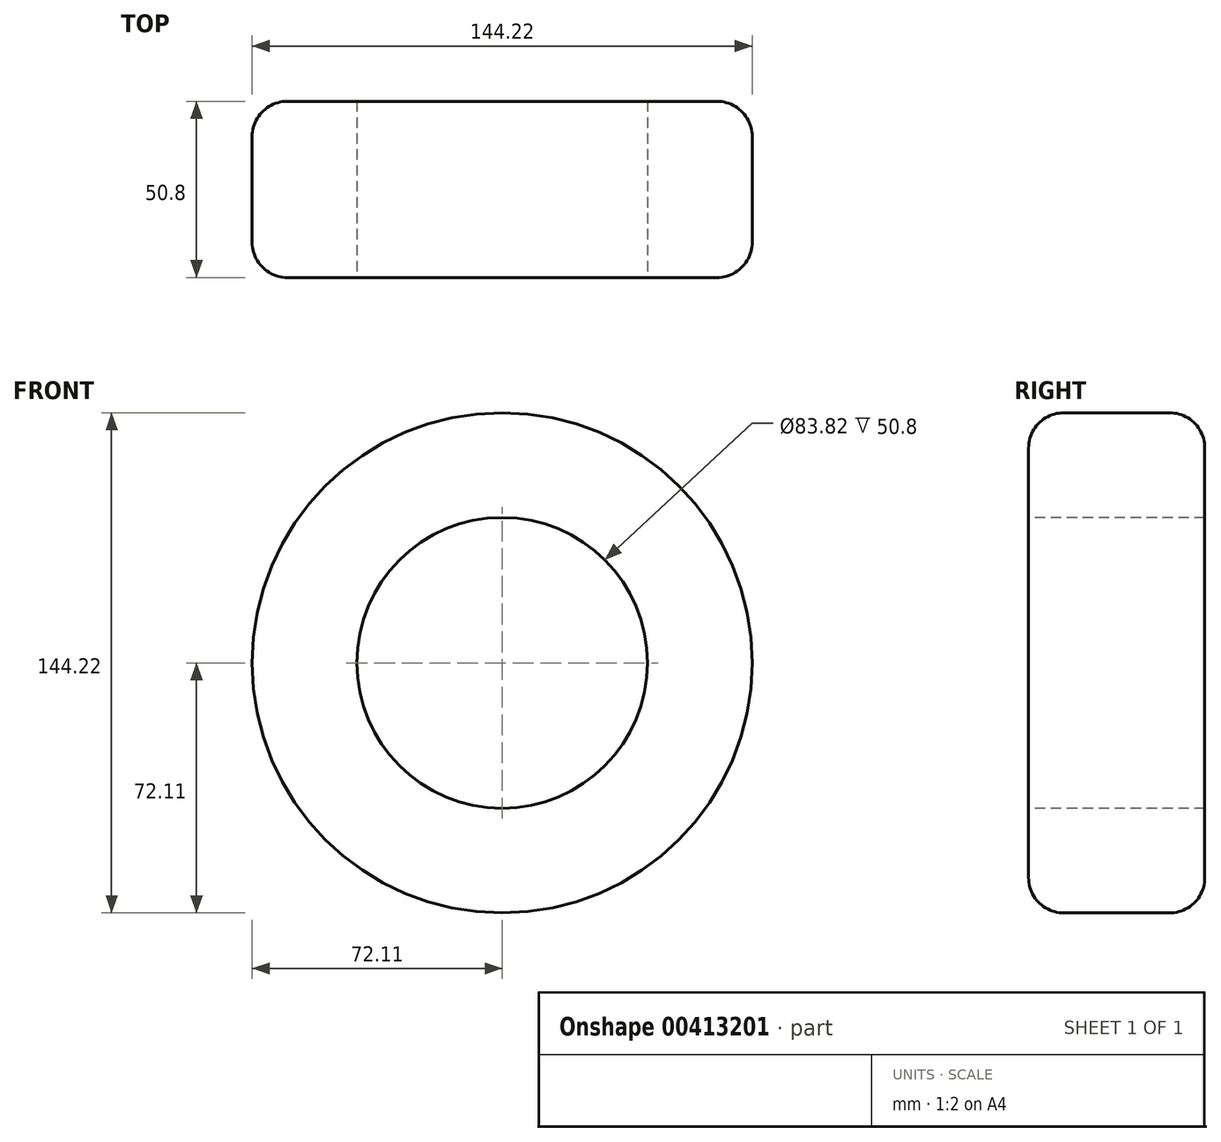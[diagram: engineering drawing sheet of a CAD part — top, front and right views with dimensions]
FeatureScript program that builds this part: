
annotation { "Feature Type Name" : "Feature", "Feature Type Description" : "" }
export const myFeature = defineFeature(function(context is Context, id is Id, definition is map)
    precondition{}
    {
        {
            var Q0;
            Q0=qCreatedBy(makeId("Front.planeOp"),FACE);
            var sketch = newSketch(context, id + "F0", { "sketchPlane" : qUnion([Q0])});
            skCircle(sketch, "E0", {"center": v(0, 0) * mm, "radius": 72.1 * mm});
            skSolve(sketch);
        }
        {
            var Q0;
            Q0=makeQuery(id+"F0.imprint","IMPRINT",FACE,{"disambiguationData":[TD([[makeQuery(id+"F0.imprint","IMPRINT",EDGE,{"derivedFrom":sQuery(id+"F0.wireOp",EDGE,"E0")}),1.0]])]});
            extrude(context, id + "F1", {"entities" : qUnion([Q0]), "depth" : 50.8 * mm});
        }
        {
            var Q0;
            Q0=makeQuery(id+"F1.opExtrude","SWEPT_FACE",FACE,{"disambiguationData":[OSD([sQuery(id+"F0.wireOp",EDGE,"E0")])]});
            fillet(context, id + "F2", {"entities" : qUnion([Q0]), "radius" : 10.16 * mm, "tangentPropagation" : true, "allowEdgeOverflow" : false});
        }
        {
            var Q0;
            Q0=makeQuery(id+"F1.opExtrude","CAP_FACE",FACE,{"disambiguationData":[OSD([sQuery(id+"F0.wireOp",EDGE,"E0")])],"isStart":false});
            var sketch = newSketch(context, id + "F3", { "sketchPlane" : qUnion([Q0])});
            skPoint(sketch, "E1", {"position": v(0, 0) * mm});
            skSolve(sketch);
        }
        {
            var Q0;
            Q0=sQuery(id+"F3.wireOp",VERTEX,"E1");
            var Q1;
            Q1=makeQuery(id+"F1.opExtrude","SWEPT_BODY",BODY,{"disambiguationData":[OSD([sQuery(id+"F0.wireOp",EDGE,"E0")])]});
            hole(context, id + "F4", {"style" : HoleStyle.SIMPLE, "endStyle" : HoleEndStyle.THROUGH, "holeDiameter" : 83.82 * mm, "isTappedThrough" : true, "tappedDepth" : 12.7 * mm, "tapClearance" : 3, "locations" : qUnion([Q0]), "scope" : qUnion([Q1])});
        }
    });
